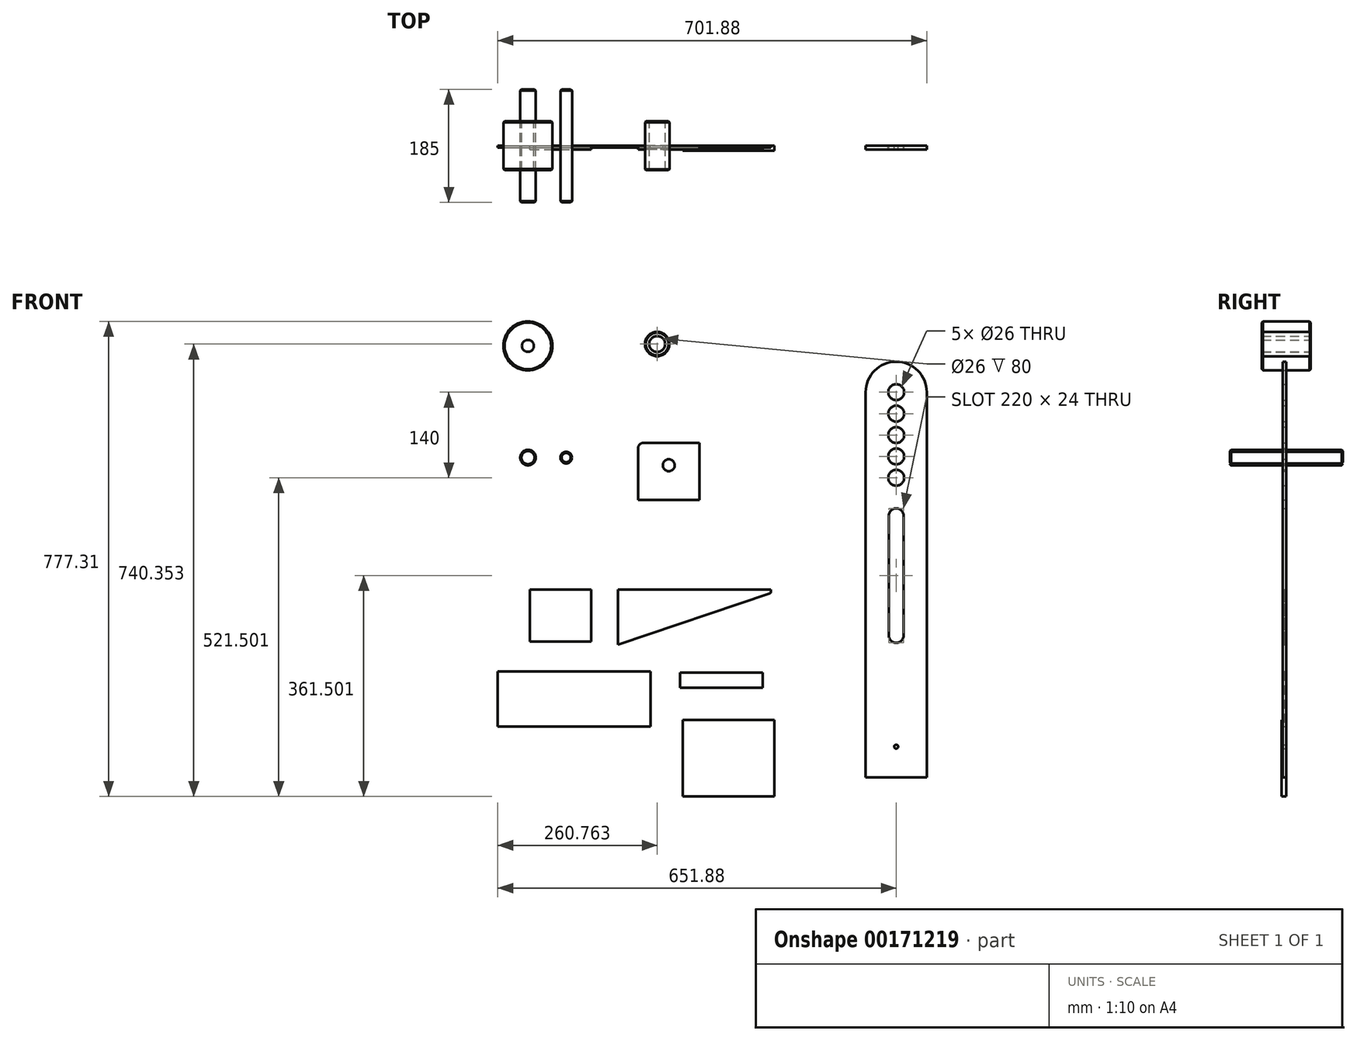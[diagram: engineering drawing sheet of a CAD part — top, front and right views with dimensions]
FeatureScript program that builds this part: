
annotation { "Feature Type Name" : "Feature", "Feature Type Description" : "" }
export const myFeature = defineFeature(function(context is Context, id is Id, definition is map)
    precondition{}
    {
        {
            var Q0;
            Q0=qCreatedBy(makeId("Front.planeOp"),FACE);
            var sketch = newSketch(context, id + "F0", { "sketchPlane" : qUnion([Q0])});
            skLineSegment(sketch, "E0", {"start": v(-50, -500.52) * mm, "end": v(50, -500.52) * mm});
            skLineSegment(sketch, "E1", {"start": v(50, -500.52) * mm, "end": v(50, 129.48) * mm});
            skLineSegment(sketch, "E2", {"start": v(-50, 129.48) * mm, "end": v(-50, -500.52) * mm});
            skArc(sketch, "E3", {"start": v(-50, 129.48) * mm, "mid": v(0, 179.48) * mm, "end": v(50, 129.48) * mm});
            skCircle(sketch, "E4", {"center": v(0, 129.48) * mm, "radius": 13 * mm});
            skCircle(sketch, "E5", {"center": v(0, 94.48) * mm, "radius": 13 * mm});
            skCircle(sketch, "E6", {"center": v(0, 59.48) * mm, "radius": 13 * mm});
            skCircle(sketch, "E7", {"center": v(0, 24.48) * mm, "radius": 13 * mm});
            skCircle(sketch, "E8", {"center": v(0, -10.52) * mm, "radius": 13 * mm});
            skCircle(sketch, "E9", {"center": v(0, -450.52) * mm, "radius": 3.25 * mm});
            skLineSegment(sketch, "E10.0", {"start": v(-12, -72.52) * mm, "end": v(-12, -268.52) * mm});
            skLineSegment(sketch, "E11.0", {"start": v(12, -72.52) * mm, "end": v(12, -268.52) * mm});
            skArc(sketch, "E12", {"start": v(12, -72.52) * mm, "mid": v(0, -60.52) * mm, "end": v(-12, -72.52) * mm});
            skArc(sketch, "E13", {"start": v(-12, -268.52) * mm, "mid": v(0, -280.52) * mm, "end": v(12, -268.52) * mm});
            skPoint(sketch, "E14.orphan", {"position": v(-50, -60.52) * mm});
            skPoint(sketch, "E15.orphan", {"position": v(-50, -72.52) * mm});
            skPoint(sketch, "E16.0.end.orphan", {"position": v(50, -60.52) * mm});
            skPoint(sketch, "E17.orphan", {"position": v(50, -72.52) * mm});
            skPoint(sketch, "E18.orphan", {"position": v(-50, -280.52) * mm});
            skPoint(sketch, "E19.orphan", {"position": v(-50, -268.52) * mm});
            skPoint(sketch, "E20.orphan", {"position": v(50, -268.52) * mm});
            skPoint(sketch, "E21.orphan", {"position": v(50, -280.52) * mm});
            skPoint(sketch, "E22.orphan", {"position": v(0, -280.52) * mm});
            skPoint(sketch, "E23.start.orphan", {"position": v(0, -60.52) * mm});
            skCircle(sketch, "E24", {"center": v(-602.68, 205.3) * mm, "radius": 9.75 * mm});
            skCircle(sketch, "E25", {"center": v(-602.68, 205.3) * mm, "radius": 40 * mm});
            skCircle(sketch, "E26", {"center": v(-391.12, 208.33) * mm, "radius": 13 * mm});
            skCircle(sketch, "E27", {"center": v(-391.12, 208.33) * mm, "radius": 20 * mm});
            skCircle(sketch, "E28", {"center": v(-602.5, 22.49) * mm, "radius": 12.7 * mm});
            skCircle(sketch, "E29", {"center": v(-540, 22.49) * mm, "radius": 9.5 * mm});
            skLineSegment(sketch, "E30.bottom", {"start": v(-322.14, 46.5) * mm, "end": v(-414.14, 46.5) * mm});
            skLineSegment(sketch, "E30.top", {"start": v(-322.14, -46.5) * mm, "end": v(-422.14, -46.5) * mm});
            skLineSegment(sketch, "E30.left", {"start": v(-322.14, 46.5) * mm, "end": v(-322.14, -46.5) * mm});
            skLineSegment(sketch, "E30.right", {"start": v(-422.14, 38.5) * mm, "end": v(-422.14, -46.5) * mm});
            skPoint(sketch, "E30.middle", {"position": v(-372.14, 0) * mm});
            skCircle(sketch, "E31", {"center": v(-372.14, 10) * mm, "radius": 9.75 * mm});
            skPoint(sketch, "E32.visualSharp", {"position": v(-422.14, 46.5) * mm});
            skArc(sketch, "E32.filletArc", {"start": v(-414.14, 46.5) * mm, "mid": v(-419.8, 44.16) * mm, "end": v(-422.14, 38.5) * mm});
            skLineSegment(sketch, "E33.bottom", {"start": v(-599.22, -278.34) * mm, "end": v(-499.22, -278.34) * mm});
            skLineSegment(sketch, "E33.top", {"start": v(-599.22, -193.34) * mm, "end": v(-499.22, -193.34) * mm});
            skLineSegment(sketch, "E33.left", {"start": v(-599.22, -278.34) * mm, "end": v(-599.22, -193.34) * mm});
            skLineSegment(sketch, "E33.right", {"start": v(-499.22, -278.34) * mm, "end": v(-499.22, -193.34) * mm});
            skLineSegment(sketch, "E34", {"start": v(-455.37, -193.34) * mm, "end": v(-205.37, -193.34) * mm});
            skLineSegment(sketch, "E35", {"start": v(-455.37, -193.34) * mm, "end": v(-455.37, -283.34) * mm});
            skLineSegment(sketch, "E36", {"start": v(-205.37, -193.34) * mm, "end": v(-205.37, -198.34) * mm});
            skLineSegment(sketch, "E37", {"start": v(-205.37, -198.34) * mm, "end": v(-207.14, -200.1) * mm});
            skLineSegment(sketch, "E38", {"start": v(-455.37, -283.34) * mm, "end": v(-207.14, -200.1) * mm});
            skLineSegment(sketch, "E39.bottom", {"start": v(-651.88, -327.58) * mm, "end": v(-401.88, -327.58) * mm});
            skLineSegment(sketch, "E39.top", {"start": v(-651.88, -417.58) * mm, "end": v(-401.88, -417.58) * mm});
            skLineSegment(sketch, "E39.left", {"start": v(-651.88, -327.58) * mm, "end": v(-651.88, -417.58) * mm});
            skLineSegment(sketch, "E39.right", {"start": v(-401.88, -327.58) * mm, "end": v(-401.88, -417.58) * mm});
            skLineSegment(sketch, "E40.bottom", {"start": v(-353.5, -329.1) * mm, "end": v(-218.5, -329.1) * mm});
            skLineSegment(sketch, "E40.top", {"start": v(-353.5, -354.1) * mm, "end": v(-218.5, -354.1) * mm});
            skLineSegment(sketch, "E40.left", {"start": v(-353.5, -329.1) * mm, "end": v(-353.5, -354.1) * mm});
            skLineSegment(sketch, "E40.right", {"start": v(-218.5, -329.1) * mm, "end": v(-218.5, -354.1) * mm});
            skLineSegment(sketch, "E41.bottom", {"start": v(-349.5, -407.02) * mm, "end": v(-199.5, -407.02) * mm});
            skLineSegment(sketch, "E41.top", {"start": v(-349.5, -532.02) * mm, "end": v(-199.5, -532.02) * mm});
            skLineSegment(sketch, "E41.left", {"start": v(-349.5, -407.02) * mm, "end": v(-349.5, -532.02) * mm});
            skLineSegment(sketch, "E41.right", {"start": v(-199.5, -407.02) * mm, "end": v(-199.5, -532.02) * mm});
            skSolve(sketch);
        }
        {
            var Q0;
            Q0=makeQuery(id+"F0.imprint","IMPRINT",FACE,{"disambiguationData":[TD([[makeQuery(id+"F0.imprint","IMPRINT",EDGE,{"derivedFrom":sQuery(id+"F0.wireOp",EDGE,"E0")}),1.0]])]});
            extrude(context, id + "F1", {"entities" : qUnion([Q0]), "depth" : 6 * mm});
        }
        {
            var Q0;
            Q0=makeQuery(id+"F0.imprint","IMPRINT",FACE,{"disambiguationData":[TD([[makeQuery(id+"F0.imprint","IMPRINT",EDGE,{"derivedFrom":sQuery(id+"F0.wireOp",EDGE,"E26")}),-1.0]])]});
            extrude(context, id + "F2", {"entities" : qUnion([Q0]), "endBound" : BoundingType.SYMMETRIC, "depth" : 80 * mm});
        }
        {
            var Q0;
            Q0=makeQuery(id+"F2.opExtrude","CAP_EDGE",EDGE,{"disambiguationData":[OSD([sQuery(id+"F0.wireOp",EDGE,"E27")])],"isStart":false});
            var Q1;
            Q1=makeQuery(id+"F2.opExtrude","CAP_EDGE",EDGE,{"disambiguationData":[OSD([sQuery(id+"F0.wireOp",EDGE,"E27")])],"isStart":true});
            chamfer(context, id + "F3", {"entities" : qUnion([Q0, Q1]), "width" : 1.5 * mm, "tangentPropagation" : true});
        }
        {
            var Q0;
            Q0=makeQuery(id+"F0.imprint","IMPRINT",FACE,{"disambiguationData":[TD([[makeQuery(id+"F0.imprint","IMPRINT",EDGE,{"derivedFrom":sQuery(id+"F0.wireOp",EDGE,"E24")}),-1.0]])]});
            extrude(context, id + "F4", {"entities" : qUnion([Q0]), "endBound" : BoundingType.SYMMETRIC, "depth" : 80 * mm});
        }
        {
            var Q0;
            Q0=makeQuery(id+"F4.opExtrude","CAP_EDGE",EDGE,{"disambiguationData":[OSD([sQuery(id+"F0.wireOp",EDGE,"E25")])],"isStart":false});
            var Q1;
            Q1=makeQuery(id+"F4.opExtrude","CAP_EDGE",EDGE,{"disambiguationData":[OSD([sQuery(id+"F0.wireOp",EDGE,"E25")])],"isStart":true});
            chamfer(context, id + "F5", {"entities" : qUnion([Q0, Q1]), "width" : 2 * mm, "tangentPropagation" : true});
        }
        {
            var Q0;
            Q0=makeQuery(id+"F0.imprint","IMPRINT",FACE,{"disambiguationData":[TD([[makeQuery(id+"F0.imprint","IMPRINT",EDGE,{"derivedFrom":sQuery(id+"F0.wireOp",EDGE,"E28")}),1.0]])]});
            extrude(context, id + "F6", {"entities" : qUnion([Q0]), "endBound" : BoundingType.SYMMETRIC, "depth" : 185 * mm});
        }
        {
            var Q0;
            Q0=makeQuery(id+"F0.imprint","IMPRINT",FACE,{"disambiguationData":[TD([[makeQuery(id+"F0.imprint","IMPRINT",EDGE,{"derivedFrom":sQuery(id+"F0.wireOp",EDGE,"E29")}),1.0]])]});
            extrude(context, id + "F7", {"entities" : qUnion([Q0]), "endBound" : BoundingType.SYMMETRIC, "depth" : 185 * mm});
        }
        {
            var Q0;
            Q0=makeQuery(id+"F6.opExtrude","CAP_EDGE",EDGE,{"disambiguationData":[OSD([sQuery(id+"F0.wireOp",EDGE,"E28")])],"isStart":false});
            var Q1;
            Q1=makeQuery(id+"F6.opExtrude","CAP_EDGE",EDGE,{"disambiguationData":[OSD([sQuery(id+"F0.wireOp",EDGE,"E28")])],"isStart":true});
            chamfer(context, id + "F8", {"entities" : qUnion([Q0, Q1]), "width" : 2 * mm, "tangentPropagation" : true});
        }
        {
            var Q0;
            Q0=makeQuery(id+"F7.opExtrude","CAP_EDGE",EDGE,{"disambiguationData":[OSD([sQuery(id+"F0.wireOp",EDGE,"E29")])],"isStart":false});
            var Q1;
            Q1=makeQuery(id+"F7.opExtrude","CAP_EDGE",EDGE,{"disambiguationData":[OSD([sQuery(id+"F0.wireOp",EDGE,"E29")])],"isStart":true});
            chamfer(context, id + "F9", {"entities" : qUnion([Q0, Q1]), "width" : 2 * mm, "tangentPropagation" : true});
        }
        {
            var Q0;
            Q0=makeQuery(id+"F0.imprint","IMPRINT",FACE,{"disambiguationData":[TD([[makeQuery(id+"F0.imprint","IMPRINT",EDGE,{"derivedFrom":sQuery(id+"F0.wireOp",EDGE,"E30.bottom")}),1.0]])]});
            extrude(context, id + "F10", {"entities" : qUnion([Q0]), "depth" : 6 * mm});
        }
        {
            var Q0;
            Q0=makeQuery(id+"F0.imprint","IMPRINT",FACE,{"disambiguationData":[TD([[makeQuery(id+"F0.imprint","IMPRINT",EDGE,{"derivedFrom":sQuery(id+"F0.wireOp",EDGE,"E41.bottom")}),-1.0]])]});
            extrude(context, id + "F11", {"entities" : qUnion([Q0]), "depth" : 8 * mm});
        }
        {
            var Q0;
            Q0=makeQuery(id+"F0.imprint","IMPRINT",FACE,{"disambiguationData":[TD([[makeQuery(id+"F0.imprint","IMPRINT",EDGE,{"derivedFrom":sQuery(id+"F0.wireOp",EDGE,"E40.bottom")}),-1.0]])]});
            extrude(context, id + "F12", {"entities" : qUnion([Q0]), "depth" : 6 * mm});
        }
        {
            var Q0;
            Q0=makeQuery(id+"F0.imprint","IMPRINT",FACE,{"disambiguationData":[TD([[makeQuery(id+"F0.imprint","IMPRINT",EDGE,{"derivedFrom":sQuery(id+"F0.wireOp",EDGE,"E34")}),-1.0]])]});
            extrude(context, id + "F13", {"entities" : qUnion([Q0]), "depth" : 3 * mm});
        }
        {
            var Q0;
            Q0=makeQuery(id+"F0.imprint","IMPRINT",FACE,{"disambiguationData":[TD([[makeQuery(id+"F0.imprint","IMPRINT",EDGE,{"derivedFrom":sQuery(id+"F0.wireOp",EDGE,"E33.bottom")}),1.0]])]});
            extrude(context, id + "F14", {"entities" : qUnion([Q0]), "depth" : 6 * mm});
        }
        {
            var Q0;
            Q0=makeQuery(id+"F0.imprint","IMPRINT",FACE,{"disambiguationData":[TD([[makeQuery(id+"F0.imprint","IMPRINT",EDGE,{"derivedFrom":sQuery(id+"F0.wireOp",EDGE,"E39.bottom")}),-1.0]])]});
            extrude(context, id + "F15", {"entities" : qUnion([Q0]), "depth" : 3 * mm});
        }
    });
